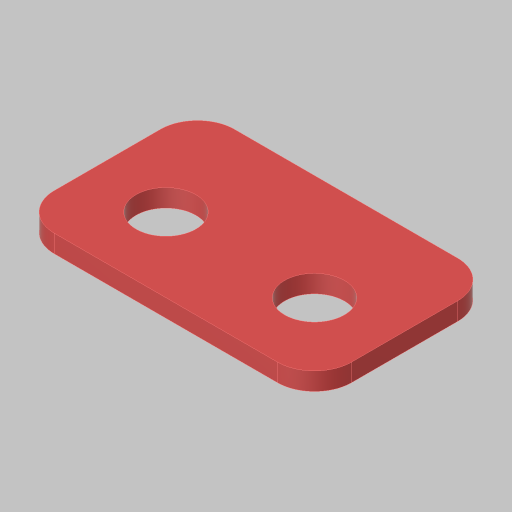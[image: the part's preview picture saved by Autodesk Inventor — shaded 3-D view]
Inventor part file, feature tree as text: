
AUTODESK INVENTOR PART (.ipt)
format: ipt  version: 2023.5 (Build 275446000, 446)  size: 161,280 bytes
history: native  units: in
note: dims shown in document units (in); Inventor stores cm internally (conversion verified against a paired STEP export)
features: sketch x2, extrude x2, fillet x2, hole x1
ambient origin geometry x8: Origin, YZ Plane, XZ Plane, XY Plane, X Axis, Y Axis, Z Axis, Center Point
bodies: Solid1 (feature_tree)
feature tree (7):
  sketch  "Sketch1"  dims[d1=0.7in d3=0.125in]
  extrude  "Extrusion1"  Depth=0.125in
  hole  "Hole1"  [1 undecoded]
  fillet  "Fillet1"  Radius=1.0in
  extrude  "Extrusion2"  Depth=0.125in
  fillet  "Fillet2"  Radius=0.25in
  sketch  "Sketch2"  dims[d4=0.197in d5=0.197in d8=1.0in d9=1.5in d10=0.25in d11=0.5in d12=0.25in d13=0.06in d14=0.0in d15=0.201in d16=0.75in d17=0.385in d18=0.25in d19=0.5635in d20=1.0in d21=0.8108in d22=0.125in d23=0.7874in d25=0.197in d26=0.3937in d28=1.0in d30=1.0in d31=1.0in d32=0.125in d33=0.0in d34=0.0in d35=0.125in]
note: 1 required parameter value undecoded (feature->parameter linkage not recoverable at this tier; creation-order binding heuristic only, values carry confidence <= 0.55)
